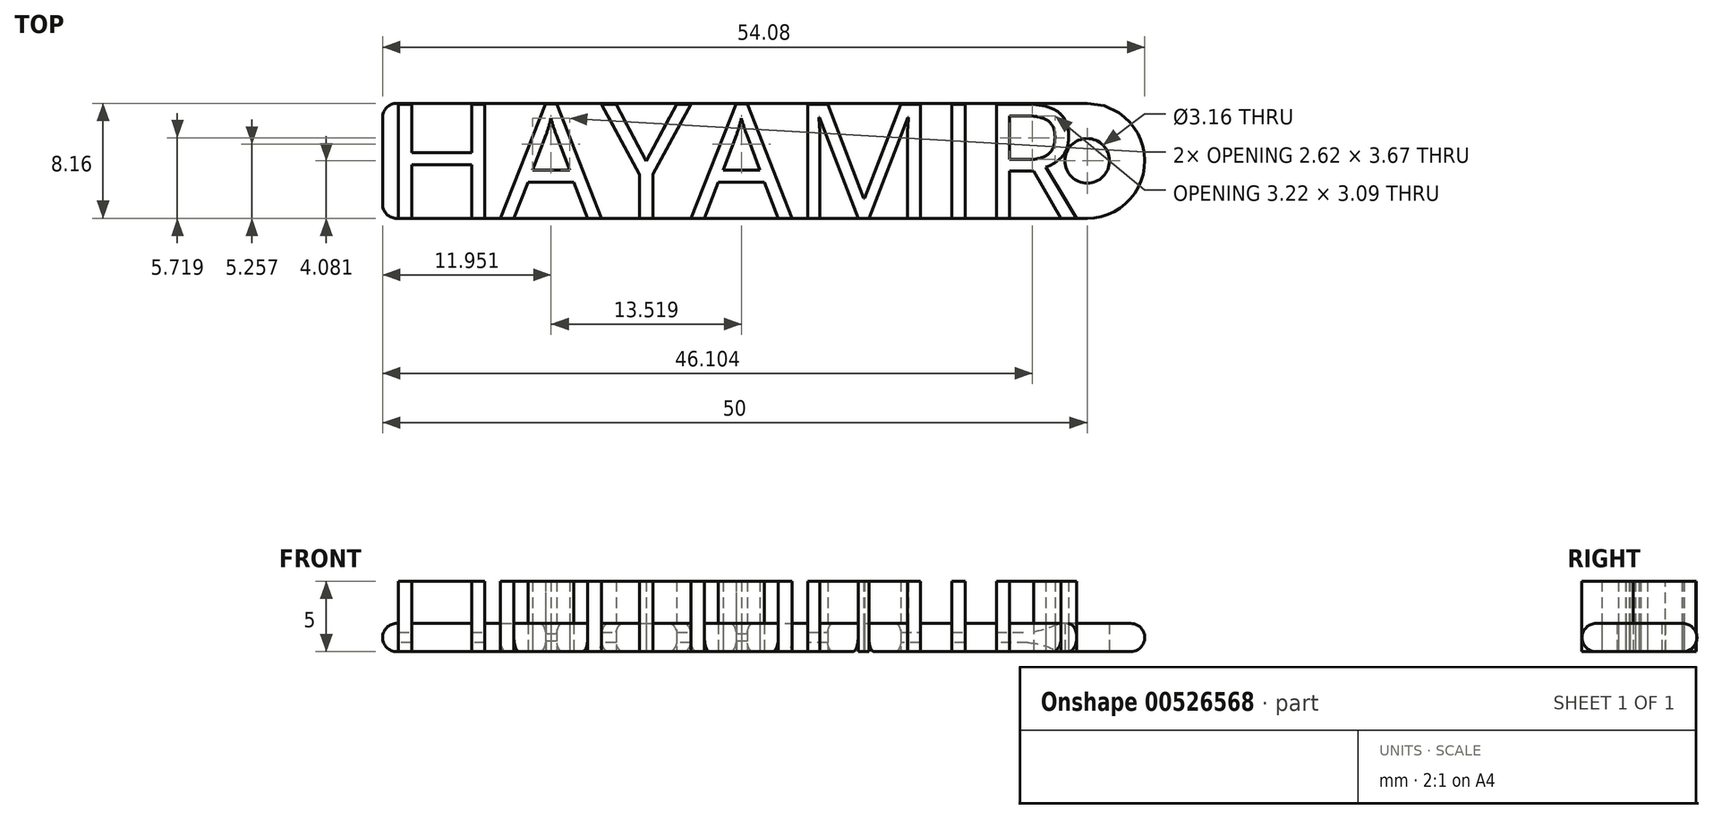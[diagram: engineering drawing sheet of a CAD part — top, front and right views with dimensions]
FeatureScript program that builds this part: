
annotation { "Feature Type Name" : "Feature", "Feature Type Description" : "" }
export const myFeature = defineFeature(function(context is Context, id is Id, definition is map)
    precondition{}
    {
        {
            var Q0;
            Q0=qCreatedBy(makeId("Top.planeOp"),FACE);
            var sketch = newSketch(context, id + "F0", { "sketchPlane" : qUnion([Q0])});
            skText(sketch, "E0", { "text": "HAYAMIR", "fontName": "OpenSans-Regular.ttf"});
            skLineSegment(sketch, "E1.bottom", {"start": v(-50, 0) * mm, "end": v(0, 0) * mm});
            skLineSegment(sketch, "E1.top", {"start": v(-50, 8.16) * mm, "end": v(0, 8.16) * mm});
            skLineSegment(sketch, "E1.left", {"start": v(-50, 0) * mm, "end": v(-50, 8.16) * mm});
            skLineSegment(sketch, "E1.right", {"start": v(0, 0) * mm, "end": v(0, 8.16) * mm});
            skArc(sketch, "E2", {"start": v(0, 0) * mm, "mid": v(4.08, 4.08) * mm, "end": v(0, 8.16) * mm});
            skCircle(sketch, "E3", {"center": v(0, 4.08) * mm, "radius": 1.58 * mm});
            const initialGuessF0  = {"E0": [-0.05, 0, 1, 0, 0.00816]};
            skSetInitialGuess(sketch, initialGuessF0);
            skSolve(sketch);
        }
        {
            var Q0;
            {var subQ1=sQuery(id+"F0.wireOp",EDGE,"E0.sketch_text.stroke-12");Q0=makeQuery(id+"F0.imprint","IMPRINT",FACE,{"disambiguationData":[TD([[makeQuery(id+"F0.imprint","IMPRINT",EDGE,{"derivedFrom":subQ1}),-1.0]])]});}
            var Q1;
            Q1=makeQuery(id+"F0.imprint","IMPRINT",FACE,{"disambiguationData":[TD([[makeQuery(id+"F0.imprint","IMPRINT",EDGE,{"derivedFrom":sQuery(id+"F0.wireOp",EDGE,"E0.sketch_text.stroke-25")}),-1.0]])]});
            var Q2;
            {var subQ1=sQuery(id+"F0.wireOp",EDGE,"E0.sketch_text.stroke-34");Q2=makeQuery(id+"F0.imprint","IMPRINT",FACE,{"disambiguationData":[TD([[makeQuery(id+"F0.imprint","IMPRINT",EDGE,{"derivedFrom":subQ1}),-1.0]])]});}
            var Q3;
            {var subQ3=sQuery(id+"F0.wireOp",EDGE,"E0.sketch_text.stroke-47");Q3=makeQuery(id+"F0.imprint","IMPRINT",FACE,{"disambiguationData":[TD([[makeQuery(id+"F0.imprint","IMPRINT",EDGE,{"derivedFrom":subQ3}),-1.0]])]});}
            var Q4;
            {var subQ0=sQuery(id+"F0.wireOp",EDGE,"E0.sketch_text.stroke-65");Q4=makeQuery(id+"F0.imprint","IMPRINT",FACE,{"disambiguationData":[TD([[makeQuery(id+"F0.imprint","IMPRINT",EDGE,{"derivedFrom":subQ0}),-1.0]])]});}
            var Q5;
            {var subQ2=sQuery(id+"F0.wireOp",EDGE,"E0.sketch_text.stroke-69");Q5=makeQuery(id+"F0.imprint","IMPRINT",FACE,{"disambiguationData":[TD([[makeQuery(id+"F0.imprint","IMPRINT",EDGE,{"derivedFrom":subQ2}),-1.0]])]});}
            var Q6;
            {var subQ2=sQuery(id+"F0.wireOp",EDGE,"E0.sketch_text.stroke-1");Q6=makeQuery(id+"F0.imprint","IMPRINT",FACE,{"disambiguationData":[TD([[makeQuery(id+"F0.imprint","IMPRINT",EDGE,{"derivedFrom":subQ2}),-1.0]])]});}
            extrude(context, id + "F1", {"entities" : qUnion([Q0, Q1, Q2, Q3, Q4, Q5, Q6]), "depth" : 5 * mm, "offsetDistance" : 25 * mm});
        }
        {
            var Q0;
            {var subQ0=sQuery(id+"F0.wireOp",EDGE,"E0.sketch_text.stroke-1");Q0=makeQuery(id+"F0.imprint","IMPRINT",FACE,{"disambiguationData":[TD([[makeQuery(id+"F0.imprint","IMPRINT",EDGE,{"derivedFrom":subQ0}),1.0]])]});}
            var Q1;
            {var subQ0=sQuery(id+"F0.wireOp",EDGE,"E2");Q1=makeQuery(id+"F0.imprint","IMPRINT",FACE,{"disambiguationData":[TD([[makeQuery(id+"F0.imprint","IMPRINT",EDGE,{"derivedFrom":subQ0}),1.0]])]});}
            var Q2;
            {var subQ19=sQuery(id+"F0.wireOp",EDGE,"E0.sketch_text.stroke-5");Q2=makeQuery(id+"F0.imprint","IMPRINT",FACE,{"disambiguationData":[TD([[makeQuery(id+"F0.imprint","IMPRINT",EDGE,{"derivedFrom":subQ19}),1.0]])]});}
            var Q3;
            Q3=makeQuery(id+"F0.imprint","IMPRINT",FACE,{"disambiguationData":[TD([[makeQuery(id+"F0.imprint","IMPRINT",EDGE,{"derivedFrom":sQuery(id+"F0.wireOp",EDGE,"E0.sketch_text.stroke-80")}),1.0]])]});
            var Q4;
            {var subQ0=sQuery(id+"F0.wireOp",EDGE,"E0.sketch_text.stroke-69");Q4=makeQuery(id+"F0.imprint","IMPRINT",FACE,{"disambiguationData":[TD([[makeQuery(id+"F0.imprint","IMPRINT",EDGE,{"derivedFrom":subQ0}),1.0]])]});}
            var Q5;
            {var subQ1=sQuery(id+"F0.wireOp",EDGE,"E0.sketch_text.stroke-60");Q5=makeQuery(id+"F0.imprint","IMPRINT",FACE,{"disambiguationData":[TD([[makeQuery(id+"F0.imprint","IMPRINT",EDGE,{"derivedFrom":subQ1}),1.0]])]});}
            var Q6;
            {var subQ1=sQuery(id+"F0.wireOp",EDGE,"E0.sketch_text.stroke-47");Q6=makeQuery(id+"F0.imprint","IMPRINT",FACE,{"disambiguationData":[TD([[makeQuery(id+"F0.imprint","IMPRINT",EDGE,{"derivedFrom":subQ1}),1.0]])]});}
            var Q7;
            {var subQ0=sQuery(id+"F0.wireOp",EDGE,"E0.sketch_text.stroke-34");Q7=makeQuery(id+"F0.imprint","IMPRINT",FACE,{"disambiguationData":[TD([[makeQuery(id+"F0.imprint","IMPRINT",EDGE,{"derivedFrom":subQ0}),1.0]])]});}
            var Q8;
            Q8=makeQuery(id+"F0.imprint","IMPRINT",FACE,{"disambiguationData":[TD([[makeQuery(id+"F0.imprint","IMPRINT",EDGE,{"derivedFrom":sQuery(id+"F0.wireOp",EDGE,"E0.sketch_text.stroke-42")}),1.0]])]});
            var Q9;
            {var subQ0=sQuery(id+"F0.wireOp",EDGE,"E0.sketch_text.stroke-12");Q9=makeQuery(id+"F0.imprint","IMPRINT",FACE,{"disambiguationData":[TD([[makeQuery(id+"F0.imprint","IMPRINT",EDGE,{"derivedFrom":subQ0}),1.0]])]});}
            var Q10;
            Q10=makeQuery(id+"F0.imprint","IMPRINT",FACE,{"disambiguationData":[TD([[makeQuery(id+"F0.imprint","IMPRINT",EDGE,{"derivedFrom":sQuery(id+"F0.wireOp",EDGE,"E0.sketch_text.stroke-20")}),1.0]])]});
            extrude(context, id + "F2", {"entities" : qUnion([Q0, Q1, Q2, Q3, Q4, Q5, Q6, Q7, Q8, Q9, Q10]), "depth" : 2 * mm, "offsetDistance" : 25 * mm});
        }
        {
            var Q0;
            Q0=makeQuery(id+"F2.opExtrude","CAP_EDGE",EDGE,{"disambiguationData":[OSD([sQuery(id+"F0.wireOp",EDGE,"E1.top")])],"isStart":false});
            var Q1;
            Q1=makeQuery(id+"F2.opExtrude","CAP_EDGE",EDGE,{"disambiguationData":[OSD([sQuery(id+"F0.wireOp",EDGE,"E1.top")])],"isStart":true});
            var Q2;
            {var subQ0=sQuery(id+"F0.wireOp",EDGE,"E1.bottom");Q2=makeQuery(id+"F2.opExtrude","CAP_EDGE",EDGE,{"disambiguationData":[OSD([subQ0]),TDD([makeQuery(id+"F0.imprint","IMPRINT",EDGE,{"disambiguationData":[TD([[makeQuery(id+"F0.imprint","INTERSECT",VERTEX,{"derivedFrom":[sQuery(id+"F0.wireOp",EDGE,"E0.sketch_text.stroke-58"),subQ0]}),-1.0]])],"derivedFrom":subQ0})])],"isStart":true});}
            var Q3;
            {var subQ0=sQuery(id+"F0.wireOp",EDGE,"E1.bottom");Q3=makeQuery(id+"F1.opExtrude","CAP_EDGE",EDGE,{"disambiguationData":[OSD([subQ0]),TDD([makeQuery(id+"F0.imprint","IMPRINT",EDGE,{"disambiguationData":[TD([[makeQuery(id+"F0.imprint","INTERSECT",VERTEX,{"derivedFrom":[sQuery(id+"F0.wireOp",EDGE,"E0.sketch_text.stroke-65"),subQ0]}),-1.0]])],"derivedFrom":subQ0})])],"isStart":true});}
            var Q4;
            {var subQ0=sQuery(id+"F0.wireOp",EDGE,"E1.bottom");Q4=makeQuery(id+"F2.opExtrude","CAP_EDGE",EDGE,{"disambiguationData":[OSD([subQ0]),TDD([makeQuery(id+"F0.imprint","IMPRINT",EDGE,{"disambiguationData":[TD([[makeQuery(id+"F0.imprint","INTERSECT",VERTEX,{"derivedFrom":[sQuery(id+"F0.wireOp",EDGE,"E0.sketch_text.stroke-67"),subQ0]}),-1.0]])],"derivedFrom":subQ0})])],"isStart":true});}
            var Q5;
            {var subQ0=sQuery(id+"F0.wireOp",EDGE,"E1.bottom");Q5=makeQuery(id+"F1.opExtrude","CAP_EDGE",EDGE,{"disambiguationData":[OSD([subQ0]),TDD([makeQuery(id+"F0.imprint","IMPRINT",EDGE,{"disambiguationData":[TD([[makeQuery(id+"F0.imprint","INTERSECT",VERTEX,{"derivedFrom":[sQuery(id+"F0.wireOp",EDGE,"E0.sketch_text.stroke-69"),subQ0]}),1.0]])],"derivedFrom":subQ0})])],"isStart":true});}
            var Q6;
            {var subQ0=sQuery(id+"F0.wireOp",EDGE,"E1.bottom");Q6=makeQuery(id+"F2.opExtrude","CAP_EDGE",EDGE,{"disambiguationData":[OSD([subQ0]),TDD([makeQuery(id+"F0.imprint","IMPRINT",EDGE,{"disambiguationData":[TD([[makeQuery(id+"F0.imprint","INTERSECT",VERTEX,{"derivedFrom":[sQuery(id+"F0.wireOp",EDGE,"E0.sketch_text.stroke-69"),subQ0]}),-1.0]])],"derivedFrom":subQ0})])],"isStart":true});}
            var Q7;
            {var subQ0=sQuery(id+"F0.wireOp",EDGE,"E1.bottom");Q7=makeQuery(id+"F1.opExtrude","CAP_EDGE",EDGE,{"disambiguationData":[OSD([subQ0]),TDD([makeQuery(id+"F0.imprint","IMPRINT",EDGE,{"disambiguationData":[TD([[makeQuery(id+"F0.imprint","INTERSECT",VERTEX,{"derivedFrom":[sQuery(id+"F0.wireOp",EDGE,"E0.sketch_text.stroke-76"),subQ0]}),1.0]])],"derivedFrom":subQ0})])],"isStart":true});}
            var Q8;
            {var subQ0=sQuery(id+"F0.wireOp",EDGE,"E1.bottom");Q8=makeQuery(id+"F2.opExtrude","CAP_EDGE",EDGE,{"disambiguationData":[OSD([subQ0]),TDD([makeQuery(id+"F0.imprint","IMPRINT",EDGE,{"disambiguationData":[TD([[makeQuery(id+"F0.imprint","INTERSECT",VERTEX,{"derivedFrom":[sQuery(id+"F0.wireOp",EDGE,"E0.sketch_text.stroke-5"),subQ0]}),1.0]])],"derivedFrom":subQ0})])],"isStart":true});}
            var Q9;
            {var subQ0=sQuery(id+"F0.wireOp",EDGE,"E1.bottom");Q9=makeQuery(id+"F2.opExtrude","CAP_EDGE",EDGE,{"disambiguationData":[OSD([subQ0]),TDD([makeQuery(id+"F0.imprint","IMPRINT",EDGE,{"disambiguationData":[TD([[makeQuery(id+"F0.imprint","INTERSECT",VERTEX,{"derivedFrom":[sQuery(id+"F0.wireOp",EDGE,"E0.sketch_text.stroke-1"),subQ0]}),1.0]])],"derivedFrom":subQ0})])],"isStart":true});}
            var Q10;
            {var subQ0=sQuery(id+"F0.wireOp",EDGE,"E1.bottom");Q10=makeQuery(id+"F1.opExtrude","CAP_EDGE",EDGE,{"disambiguationData":[OSD([subQ0]),TDD([makeQuery(id+"F0.imprint","IMPRINT",EDGE,{"disambiguationData":[TD([[makeQuery(id+"F0.imprint","INTERSECT",VERTEX,{"derivedFrom":[sQuery(id+"F0.wireOp",EDGE,"E0.sketch_text.stroke-1"),subQ0]}),-1.0]])],"derivedFrom":subQ0})])],"isStart":true});}
            var Q11;
            {var subQ0=sQuery(id+"F0.wireOp",EDGE,"E1.bottom");Q11=makeQuery(id+"F2.opExtrude","CAP_EDGE",EDGE,{"disambiguationData":[OSD([subQ0]),TDD([makeQuery(id+"F0.imprint","IMPRINT",EDGE,{"disambiguationData":[TD([[makeQuery(id+"F0.imprint","INTERSECT",VERTEX,{"derivedFrom":[sQuery(id+"F0.wireOp",EDGE,"E0.sketch_text.stroke-11"),subQ0]}),-1.0]])],"derivedFrom":subQ0})])],"isStart":true});}
            var Q12;
            {var subQ0=sQuery(id+"F0.wireOp",EDGE,"E1.bottom");Q12=makeQuery(id+"F1.opExtrude","CAP_EDGE",EDGE,{"disambiguationData":[OSD([subQ0]),TDD([makeQuery(id+"F0.imprint","IMPRINT",EDGE,{"disambiguationData":[TD([[makeQuery(id+"F0.imprint","INTERSECT",VERTEX,{"derivedFrom":[sQuery(id+"F0.wireOp",EDGE,"E0.sketch_text.stroke-14"),subQ0]}),1.0]])],"derivedFrom":subQ0})])],"isStart":true});}
            var Q13;
            {var subQ0=sQuery(id+"F0.wireOp",EDGE,"E1.bottom");Q13=makeQuery(id+"F2.opExtrude","CAP_EDGE",EDGE,{"disambiguationData":[OSD([subQ0]),TDD([makeQuery(id+"F0.imprint","IMPRINT",EDGE,{"disambiguationData":[TD([[makeQuery(id+"F0.imprint","INTERSECT",VERTEX,{"derivedFrom":[sQuery(id+"F0.wireOp",EDGE,"E0.sketch_text.stroke-12"),subQ0]}),1.0]])],"derivedFrom":subQ0})])],"isStart":true});}
            var Q14;
            {var subQ0=sQuery(id+"F0.wireOp",EDGE,"E1.bottom");Q14=makeQuery(id+"F1.opExtrude","CAP_EDGE",EDGE,{"disambiguationData":[OSD([subQ0]),TDD([makeQuery(id+"F0.imprint","IMPRINT",EDGE,{"disambiguationData":[TD([[makeQuery(id+"F0.imprint","INTERSECT",VERTEX,{"derivedFrom":[sQuery(id+"F0.wireOp",EDGE,"E0.sketch_text.stroke-12"),subQ0]}),-1.0]])],"derivedFrom":subQ0})])],"isStart":true});}
            var Q15;
            {var subQ0=sQuery(id+"F0.wireOp",EDGE,"E1.bottom");Q15=makeQuery(id+"F2.opExtrude","CAP_EDGE",EDGE,{"disambiguationData":[OSD([subQ0]),TDD([makeQuery(id+"F0.imprint","IMPRINT",EDGE,{"disambiguationData":[TD([[makeQuery(id+"F0.imprint","INTERSECT",VERTEX,{"derivedFrom":[sQuery(id+"F0.wireOp",EDGE,"E0.sketch_text.stroke-18"),subQ0]}),-1.0]])],"derivedFrom":subQ0})])],"isStart":true});}
            var Q16;
            {var subQ0=sQuery(id+"F0.wireOp",EDGE,"E1.bottom");Q16=makeQuery(id+"F1.opExtrude","CAP_EDGE",EDGE,{"disambiguationData":[OSD([subQ0]),TDD([makeQuery(id+"F0.imprint","IMPRINT",EDGE,{"disambiguationData":[TD([[makeQuery(id+"F0.imprint","INTERSECT",VERTEX,{"derivedFrom":[sQuery(id+"F0.wireOp",EDGE,"E0.sketch_text.stroke-28"),subQ0]}),1.0]])],"derivedFrom":subQ0})])],"isStart":true});}
            var Q17;
            {var subQ0=sQuery(id+"F0.wireOp",EDGE,"E1.bottom");Q17=makeQuery(id+"F2.opExtrude","CAP_EDGE",EDGE,{"disambiguationData":[OSD([subQ0]),TDD([makeQuery(id+"F0.imprint","IMPRINT",EDGE,{"disambiguationData":[TD([[makeQuery(id+"F0.imprint","INTERSECT",VERTEX,{"derivedFrom":[sQuery(id+"F0.wireOp",EDGE,"E0.sketch_text.stroke-28"),subQ0]}),-1.0]])],"derivedFrom":subQ0})])],"isStart":true});}
            var Q18;
            {var subQ0=sQuery(id+"F0.wireOp",EDGE,"E1.bottom");Q18=makeQuery(id+"F1.opExtrude","CAP_EDGE",EDGE,{"disambiguationData":[OSD([subQ0]),TDD([makeQuery(id+"F0.imprint","IMPRINT",EDGE,{"disambiguationData":[TD([[makeQuery(id+"F0.imprint","INTERSECT",VERTEX,{"derivedFrom":[sQuery(id+"F0.wireOp",EDGE,"E0.sketch_text.stroke-36"),subQ0]}),1.0]])],"derivedFrom":subQ0})])],"isStart":true});}
            var Q19;
            {var subQ0=sQuery(id+"F0.wireOp",EDGE,"E1.bottom");Q19=makeQuery(id+"F2.opExtrude","CAP_EDGE",EDGE,{"disambiguationData":[OSD([subQ0]),TDD([makeQuery(id+"F0.imprint","IMPRINT",EDGE,{"disambiguationData":[TD([[makeQuery(id+"F0.imprint","INTERSECT",VERTEX,{"derivedFrom":[sQuery(id+"F0.wireOp",EDGE,"E0.sketch_text.stroke-34"),subQ0]}),1.0]])],"derivedFrom":subQ0})])],"isStart":true});}
            var Q20;
            {var subQ0=sQuery(id+"F0.wireOp",EDGE,"E1.bottom");Q20=makeQuery(id+"F1.opExtrude","CAP_EDGE",EDGE,{"disambiguationData":[OSD([subQ0]),TDD([makeQuery(id+"F0.imprint","IMPRINT",EDGE,{"disambiguationData":[TD([[makeQuery(id+"F0.imprint","INTERSECT",VERTEX,{"derivedFrom":[sQuery(id+"F0.wireOp",EDGE,"E0.sketch_text.stroke-34"),subQ0]}),-1.0]])],"derivedFrom":subQ0})])],"isStart":true});}
            var Q21;
            {var subQ0=sQuery(id+"F0.wireOp",EDGE,"E1.bottom");Q21=makeQuery(id+"F1.opExtrude","CAP_EDGE",EDGE,{"disambiguationData":[OSD([subQ0]),TDD([makeQuery(id+"F0.imprint","IMPRINT",EDGE,{"disambiguationData":[TD([[makeQuery(id+"F0.imprint","INTERSECT",VERTEX,{"derivedFrom":[sQuery(id+"F0.wireOp",EDGE,"E0.sketch_text.stroke-50"),subQ0]}),1.0]])],"derivedFrom":subQ0})])],"isStart":true});}
            var Q22;
            {var subQ0=sQuery(id+"F0.wireOp",EDGE,"E1.bottom");Q22=makeQuery(id+"F2.opExtrude","CAP_EDGE",EDGE,{"disambiguationData":[OSD([subQ0]),TDD([makeQuery(id+"F0.imprint","IMPRINT",EDGE,{"disambiguationData":[TD([[makeQuery(id+"F0.imprint","INTERSECT",VERTEX,{"derivedFrom":[sQuery(id+"F0.wireOp",EDGE,"E0.sketch_text.stroke-47"),subQ0]}),1.0]])],"derivedFrom":subQ0})])],"isStart":true});}
            var Q23;
            {var subQ0=sQuery(id+"F0.wireOp",EDGE,"E1.bottom");Q23=makeQuery(id+"F1.opExtrude","CAP_EDGE",EDGE,{"disambiguationData":[OSD([subQ0]),TDD([makeQuery(id+"F0.imprint","IMPRINT",EDGE,{"disambiguationData":[TD([[makeQuery(id+"F0.imprint","INTERSECT",VERTEX,{"derivedFrom":[sQuery(id+"F0.wireOp",EDGE,"E0.sketch_text.stroke-47"),subQ0]}),-1.0]])],"derivedFrom":subQ0})])],"isStart":true});}
            var Q24;
            {var subQ0=sQuery(id+"F0.wireOp",EDGE,"E1.bottom");Q24=makeQuery(id+"F2.opExtrude","CAP_EDGE",EDGE,{"disambiguationData":[OSD([subQ0]),TDD([makeQuery(id+"F0.imprint","IMPRINT",EDGE,{"disambiguationData":[TD([[makeQuery(id+"F0.imprint","INTERSECT",VERTEX,{"derivedFrom":[sQuery(id+"F0.wireOp",EDGE,"E0.sketch_text.stroke-60"),subQ0]}),1.0]])],"derivedFrom":subQ0})])],"isStart":true});}
            var Q25;
            {var subQ0=sQuery(id+"F0.wireOp",EDGE,"E1.bottom");Q25=makeQuery(id+"F1.opExtrude","CAP_EDGE",EDGE,{"disambiguationData":[OSD([subQ0]),TDD([makeQuery(id+"F0.imprint","IMPRINT",EDGE,{"disambiguationData":[TD([[makeQuery(id+"F0.imprint","INTERSECT",VERTEX,{"derivedFrom":[sQuery(id+"F0.wireOp",EDGE,"E0.sketch_text.stroke-58"),subQ0]}),1.0]])],"derivedFrom":subQ0})])],"isStart":true});}
            var Q26;
            Q26=makeQuery(id+"F2.opExtrude","CAP_EDGE",EDGE,{"disambiguationData":[OSD([sQuery(id+"F0.wireOp",EDGE,"E1.left")])],"isStart":true});
            var Q27;
            Q27=makeQuery(id+"F2.opExtrude","SWEPT_EDGE",EDGE,{"disambiguationData":[OSD([sQuery(id+"F0.wireOp",EDGE,"E1.bottom"),sQuery(id+"F0.wireOp",EDGE,"E1.left")])]});
            var Q28;
            Q28=makeQuery(id+"F2.opExtrude","SWEPT_EDGE",EDGE,{"disambiguationData":[OSD([sQuery(id+"F0.wireOp",EDGE,"E1.top"),sQuery(id+"F0.wireOp",EDGE,"E1.left")])]});
            var Q29;
            Q29=makeQuery(id+"F2.opExtrude","CAP_EDGE",EDGE,{"disambiguationData":[OSD([sQuery(id+"F0.wireOp",EDGE,"E1.left")])],"isStart":false});
            var Q30;
            {var subQ0=sQuery(id+"F0.wireOp",EDGE,"E1.bottom");Q30=makeQuery(id+"F2.opExtrude","CAP_EDGE",EDGE,{"disambiguationData":[OSD([subQ0]),TDD([makeQuery(id+"F0.imprint","IMPRINT",EDGE,{"disambiguationData":[TD([[makeQuery(id+"F0.imprint","INTERSECT",VERTEX,{"derivedFrom":[sQuery(id+"F0.wireOp",EDGE,"E0.sketch_text.stroke-5"),subQ0]}),1.0]])],"derivedFrom":subQ0})])],"isStart":false});}
            var Q31;
            {var subQ0=sQuery(id+"F0.wireOp",EDGE,"E1.bottom");Q31=makeQuery(id+"F2.opExtrude","CAP_EDGE",EDGE,{"disambiguationData":[OSD([subQ0]),TDD([makeQuery(id+"F0.imprint","IMPRINT",EDGE,{"disambiguationData":[TD([[makeQuery(id+"F0.imprint","INTERSECT",VERTEX,{"derivedFrom":[sQuery(id+"F0.wireOp",EDGE,"E0.sketch_text.stroke-40"),subQ0]}),-1.0]])],"derivedFrom":subQ0})])],"isStart":true});}
            var Q32;
            {var subQ0=sQuery(id+"F0.wireOp",EDGE,"E1.bottom");Q32=makeQuery(id+"F1.opExtrude","CAP_EDGE",EDGE,{"disambiguationData":[OSD([subQ0]),TDD([makeQuery(id+"F0.imprint","IMPRINT",EDGE,{"disambiguationData":[TD([[makeQuery(id+"F0.imprint","INTERSECT",VERTEX,{"derivedFrom":[sQuery(id+"F0.wireOp",EDGE,"E0.sketch_text.stroke-3"),subQ0]}),1.0]])],"derivedFrom":subQ0})])],"isStart":true});}
            fillet(context, id + "F3", {"entities" : qUnion([Q0, Q1, Q2, Q3, Q4, Q5, Q6, Q7, Q8, Q9, Q10, Q11, Q12, Q13, Q14, Q15, Q16, Q17, Q18, Q19, Q20, Q21, Q22, Q23, Q24, Q25, Q26, Q27, Q28, Q29, Q30, Q31, Q32]), "radius" : 1 * mm, "tangentPropagation" : true, "allowEdgeOverflow" : false});
        }
    });
